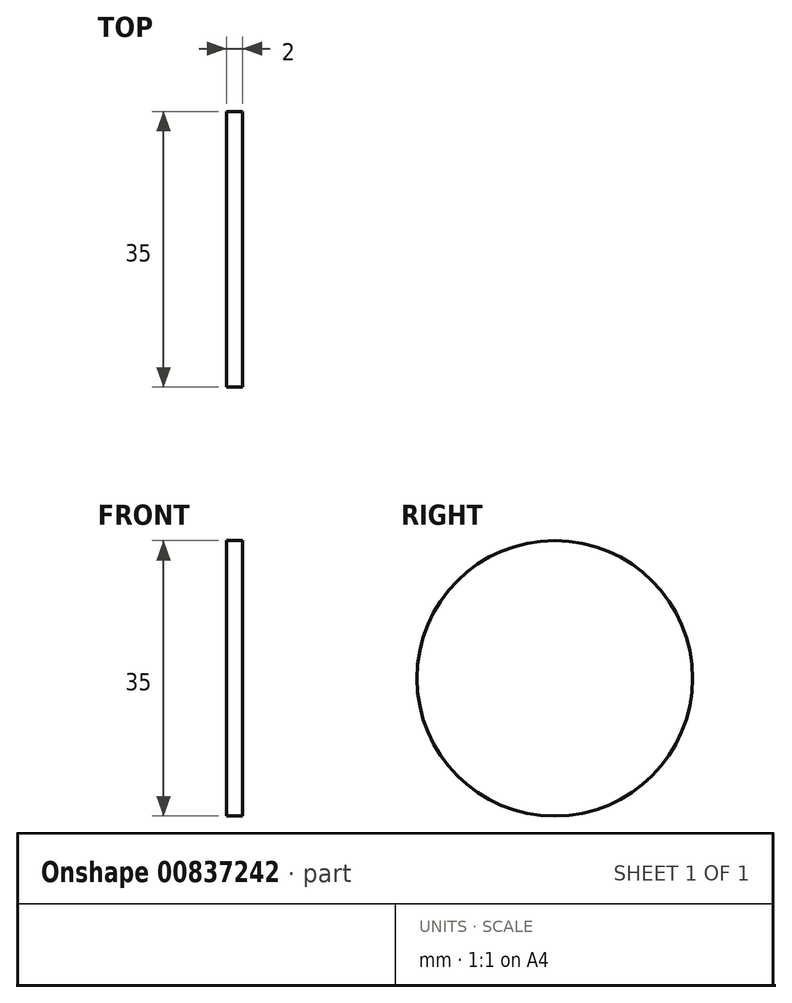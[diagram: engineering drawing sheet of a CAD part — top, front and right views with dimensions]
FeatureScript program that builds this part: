
annotation { "Feature Type Name" : "Feature", "Feature Type Description" : "" }
export const myFeature = defineFeature(function(context is Context, id is Id, definition is map)
    precondition{}
    {
        {
            var Q0;
            Q0=qCreatedBy(makeId("Right.planeOp"),FACE);
            var sketch = newSketch(context, id + "F0", { "sketchPlane" : qUnion([Q0])});
            skCircle(sketch, "E0", {"center": v(0, 0) * mm, "radius": 17.5 * mm});
            skSolve(sketch);
        }
        {
            var Q0;
            Q0 = qSketchRegion(id + "F0", true);
            extrude(context, id + "F1", {"entities" : qUnion([Q0]), "depth" : 2 * mm, "offsetDistance" : 25.4 * mm});
        }
    });
